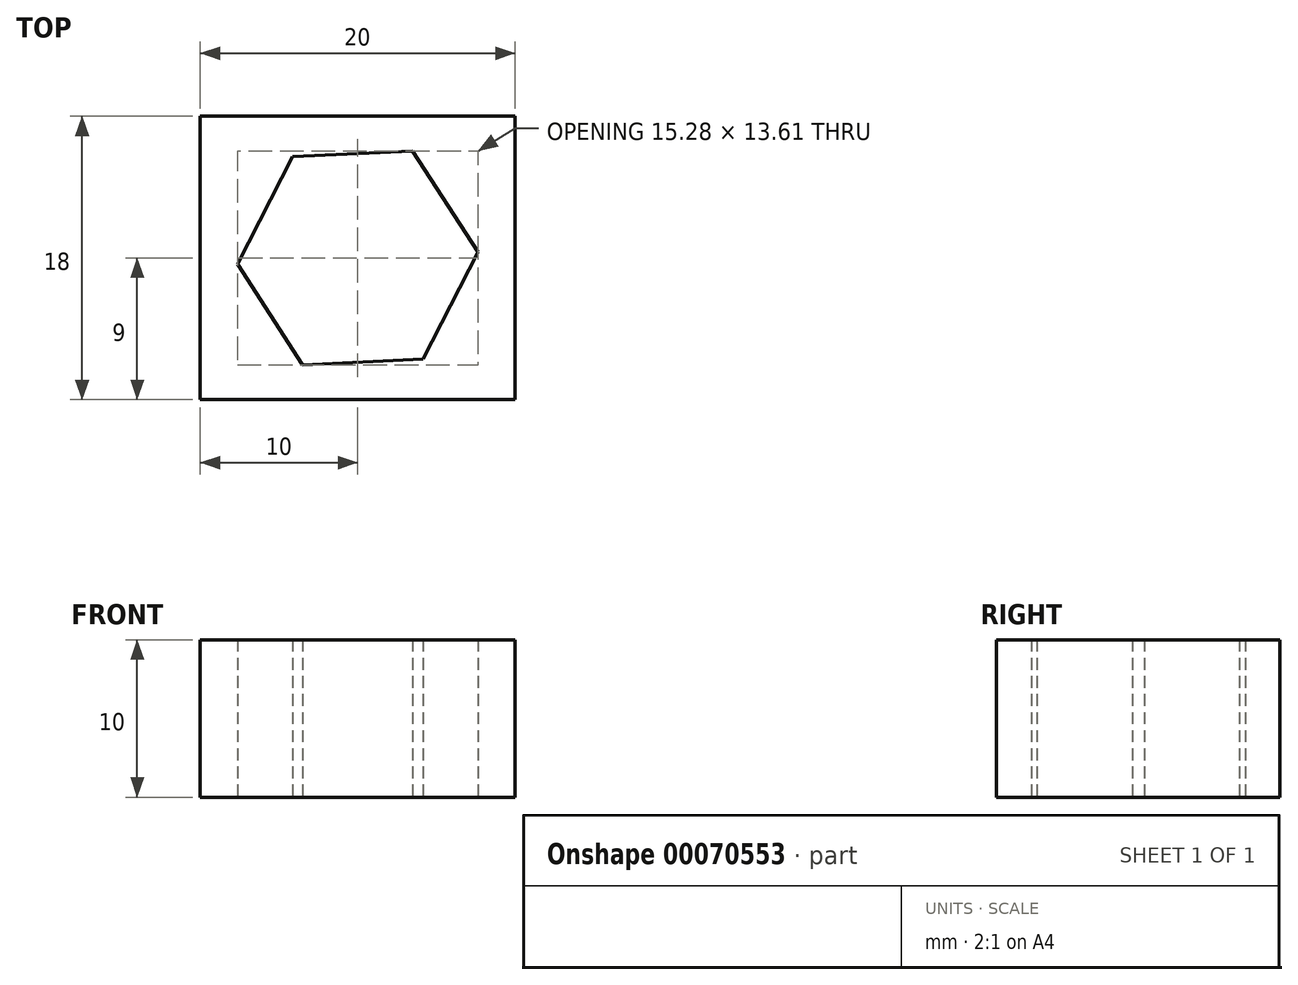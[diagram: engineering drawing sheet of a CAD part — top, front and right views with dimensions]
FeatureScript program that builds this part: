
annotation { "Feature Type Name" : "Feature", "Feature Type Description" : "" }
export const myFeature = defineFeature(function(context is Context, id is Id, definition is map)
    precondition{}
    {
        {
            var Q0;
            Q0=qCreatedBy(makeId("Top.planeOp"),FACE);
            var sketch = newSketch(context, id + "F0", { "sketchPlane" : qUnion([Q0])});
            skCircle(sketch, "E0.cCircle", {"center": v(0, 0) * mm, "radius": 6.62 * mm, "construction": true});
            skLineSegment(sketch, "E0.0", {"start": v(3.5, 6.8) * mm, "end": v(7.64, 0.37) * mm});
            skLineSegment(sketch, "E0.1", {"start": v(7.64, 0.37) * mm, "end": v(4.14, -6.43) * mm});
            skLineSegment(sketch, "E0.2", {"start": v(4.14, -6.43) * mm, "end": v(-3.5, -6.8) * mm});
            skLineSegment(sketch, "E0.3", {"start": v(-3.5, -6.8) * mm, "end": v(-7.64, -0.37) * mm});
            skLineSegment(sketch, "E0.4", {"start": v(-7.64, -0.37) * mm, "end": v(-4.14, 6.43) * mm});
            skLineSegment(sketch, "E0.5", {"start": v(-4.14, 6.43) * mm, "end": v(3.5, 6.8) * mm});
            skPoint(sketch, "E0.0.midPoint", {"position": v(5.57, 3.59) * mm});
            skLineSegment(sketch, "E1.rect.bottom", {"start": v(10, 9) * mm, "end": v(-10, 9) * mm});
            skLineSegment(sketch, "E1.rect.top", {"start": v(10, -9) * mm, "end": v(-10, -9) * mm});
            skLineSegment(sketch, "E1.rect.left", {"start": v(10, 9) * mm, "end": v(10, -9) * mm});
            skLineSegment(sketch, "E1.rect.right", {"start": v(-10, 9) * mm, "end": v(-10, -9) * mm});
            skSolve(sketch);
        }
        {
            var Q0;
            Q0=makeQuery(id+"F0.imprint","IMPRINT",FACE,{"disambiguationData":[TD([[makeQuery(id+"F0.imprint","IMPRINT",EDGE,{"derivedFrom":sQuery(id+"F0.wireOp",EDGE,"E0.0")}),1.0]])]});
            extrude(context, id + "F1", {"entities" : qUnion([Q0]), "depth" : 10 * mm});
        }
    });
